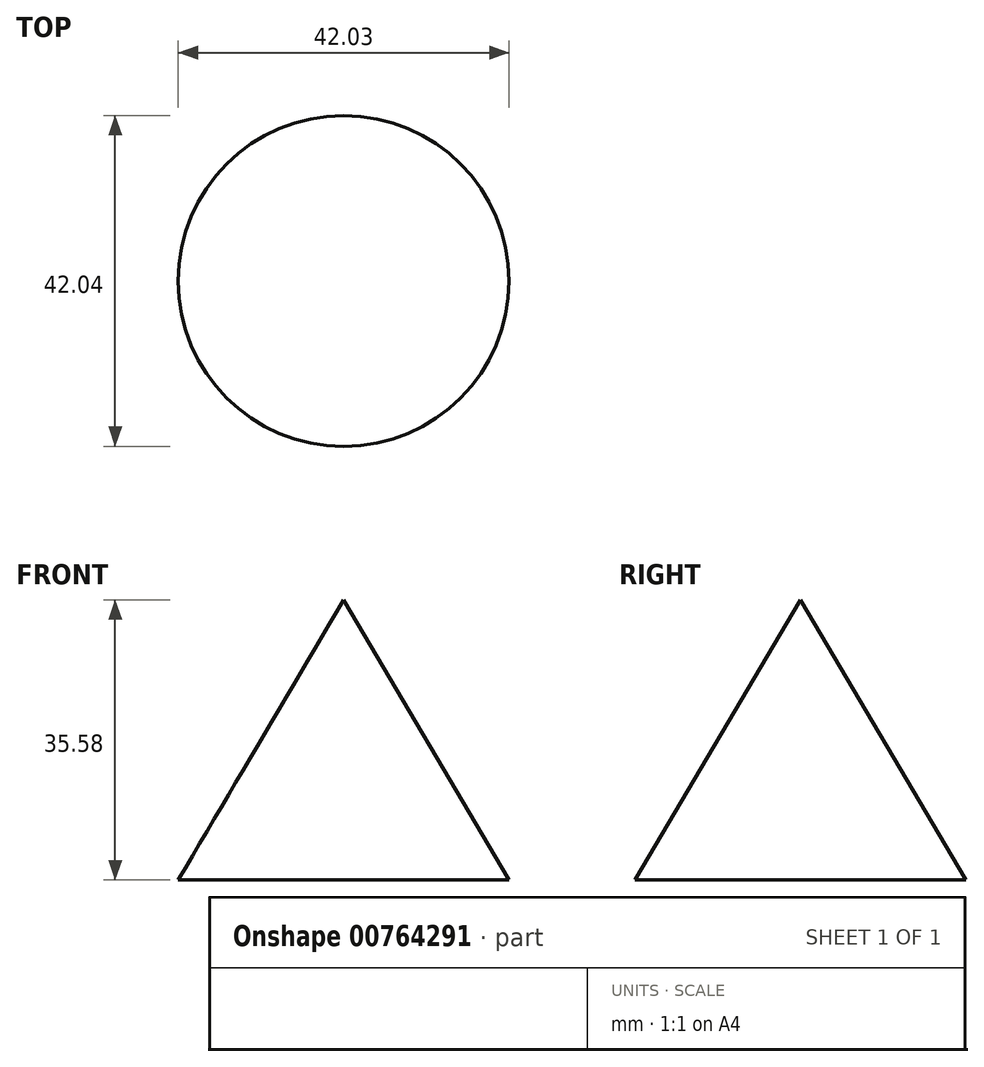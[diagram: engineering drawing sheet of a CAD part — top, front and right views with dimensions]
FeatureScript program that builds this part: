
annotation { "Feature Type Name" : "Feature", "Feature Type Description" : "" }
export const myFeature = defineFeature(function(context is Context, id is Id, definition is map)
    precondition{}
    {
        {
            var Q0;
            Q0=qCreatedBy(makeId("Front.planeOp"),FACE);
            var sketch = newSketch(context, id + "F0", { "sketchPlane" : qUnion([Q0])});
            skLineSegment(sketch, "E0", {"start": v(-34.94, 33.1) * mm, "end": v(-34.94, -2.49) * mm});
            skLineSegment(sketch, "E1", {"start": v(-34.94, -2.49) * mm, "end": v(-13.92, -2.49) * mm});
            skLineSegment(sketch, "E2", {"start": v(-13.92, -2.49) * mm, "end": v(-34.94, 33.1) * mm});
            skSolve(sketch);
        }
        {
            var Q0;
            Q0=makeQuery(id+"F0.imprint","IMPRINT",FACE,{"disambiguationData":[TD([[makeQuery(id+"F0.imprint","IMPRINT",EDGE,{"derivedFrom":sQuery(id+"F0.wireOp",EDGE,"E0")}),1.0]])]});
            var Q1;
            Q1=sQuery(id+"F0.wireOp",EDGE,"E0");
            revolve(context, id + "F1", {"surfaceOperationType" : NewSurfaceOperationType.NEW, "entities" : qUnion([Q0]), "axis" : qUnion([Q1]), "revolveType" : RevolveType.FULL});
        }
        {
            var Q0;
            Q0=qCreatedBy(makeId("Top.planeOp"),FACE);
            var sketch = newSketch(context, id + "F2", { "sketchPlane" : qUnion([Q0])});
            skLineSegment(sketch, "E3", {"start": v(-45.35, 31.32) * mm, "end": v(-45.35, -29.08) * mm});
            skSolve(sketch);
        }
        {
            var Q0;
            Q0=sQuery(id+"F2.wireOp",EDGE,"E3");
            extrude(context, id + "F3", {"bodyType" : ToolBodyType.SURFACE, "surfaceEntities" : qUnion([Q0]), "endBound" : BoundingType.SYMMETRIC, "depth" : 81.89 * mm, "offsetDistance" : 25.4 * mm});
        }
        {
            var Q0;
            Q0=qCreatedBy(makeId("Right.planeOp"),FACE);
            var sketch = newSketch(context, id + "F4", { "sketchPlane" : qUnion([Q0])});
            skLineSegment(sketch, "E4", {"start": v(-46.18, 23.69) * mm, "end": v(40.1, 23.69) * mm});
            skSolve(sketch);
        }
        {
            var Q0;
            Q0=sQuery(id+"F4.wireOp",EDGE,"E4");
            extrude(context, id + "F5", {"bodyType" : ToolBodyType.SURFACE, "surfaceEntities" : qUnion([Q0]), "endBound" : BoundingType.SYMMETRIC, "depth" : 107.19 * mm, "offsetDistance" : 25.4 * mm});
        }
    });
